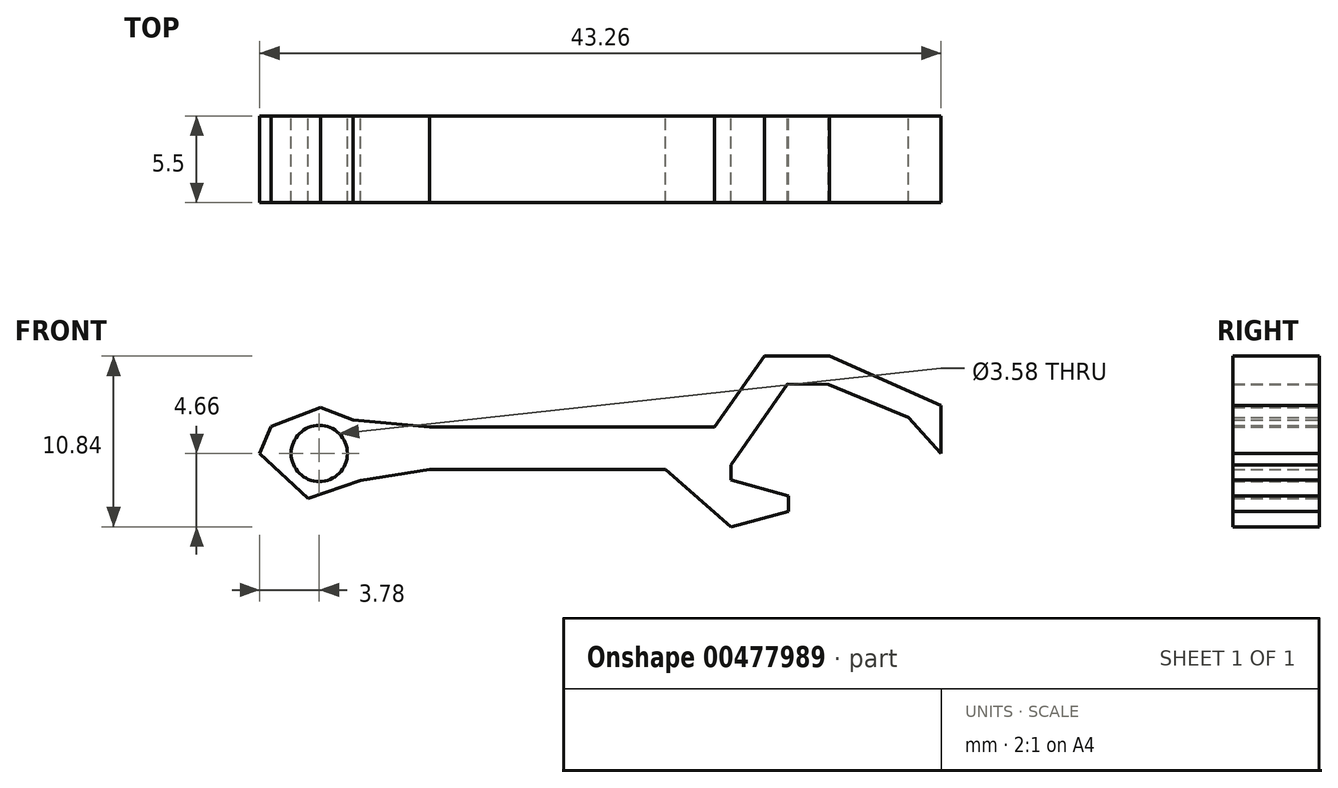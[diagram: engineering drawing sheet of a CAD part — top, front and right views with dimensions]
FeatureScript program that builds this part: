
annotation { "Feature Type Name" : "Feature", "Feature Type Description" : "" }
export const myFeature = defineFeature(function(context is Context, id is Id, definition is map)
    precondition{}
    {
        {
            var Q0;
            Q0=qCreatedBy(makeId("Front.planeOp"),FACE);
            var sketch = newSketch(context, id + "F0", { "sketchPlane" : qUnion([Q0])});
            skLineSegment(sketch, "E0", {"start": v(21.75, 0) * mm, "end": v(19.68, 2.28) * mm});
            skLineSegment(sketch, "E1", {"start": v(8.42, -0.72) * mm, "end": v(8.42, -1.68) * mm});
            skLineSegment(sketch, "E2", {"start": v(8.42, -1.68) * mm, "end": v(12.08, -2.7) * mm});
            skLineSegment(sketch, "E3", {"start": v(12.08, -2.7) * mm, "end": v(12.08, -3.68) * mm});
            skLineSegment(sketch, "E4", {"start": v(12.08, -3.68) * mm, "end": v(8.42, -4.66) * mm});
            skLineSegment(sketch, "E5", {"start": v(8.42, -4.66) * mm, "end": v(4.26, -1.03) * mm});
            skLineSegment(sketch, "E6.0", {"start": v(19.68, 2.28) * mm, "end": v(14.6, 4.38) * mm});
            skLineSegment(sketch, "E7.0", {"start": v(14.6, 4.38) * mm, "end": v(12, 4.4) * mm});
            skLineSegment(sketch, "E8", {"start": v(8.42, -0.72) * mm, "end": v(12, 4.4) * mm});
            skLineSegment(sketch, "E9", {"start": v(7.38, 1.68) * mm, "end": v(10.53, 6.18) * mm});
            skLineSegment(sketch, "E10", {"start": v(10.53, 6.18) * mm, "end": v(14.66, 6.18) * mm});
            skLineSegment(sketch, "E11", {"start": v(14.66, 6.18) * mm, "end": v(21.75, 3.05) * mm});
            skLineSegment(sketch, "E12", {"start": v(21.75, 3.05) * mm, "end": v(21.75, 0) * mm});
            skLineSegment(sketch, "E13", {"start": v(7.38, 1.68) * mm, "end": v(-10.71, 1.68) * mm});
            skLineSegment(sketch, "E14", {"start": v(4.26, -1.03) * mm, "end": v(-10.71, -1.03) * mm});
            skLineSegment(sketch, "E15", {"start": v(-17.65, 2.92) * mm, "end": v(-20.8, 1.7) * mm});
            skLineSegment(sketch, "E16", {"start": v(-20.8, 1.7) * mm, "end": v(-21.51, 0) * mm});
            skLineSegment(sketch, "E17", {"start": v(-21.51, 0) * mm, "end": v(-18.46, -2.85) * mm});
            skLineSegment(sketch, "E18", {"start": v(-18.46, -2.85) * mm, "end": v(-15.12, -1.7) * mm});
            skLineSegment(sketch, "E19", {"start": v(-15.58, 2.14) * mm, "end": v(-17.65, 2.92) * mm});
            skLineSegment(sketch, "E20", {"start": v(-15.12, -1.7) * mm, "end": v(-10.71, -1.03) * mm});
            skLineSegment(sketch, "E21", {"start": v(-15.58, 2.14) * mm, "end": v(-10.71, 1.68) * mm});
            skCircle(sketch, "E22", {"center": v(-17.73, 0) * mm, "radius": 1.79 * mm});
            skSolve(sketch);
        }
        {
            var Q0;
            Q0=makeQuery(id+"F0.imprint","IMPRINT",FACE,{"disambiguationData":[TD([[makeQuery(id+"F0.imprint","IMPRINT",EDGE,{"derivedFrom":sQuery(id+"F0.wireOp",EDGE,"E0")}),-1.0]])]});
            extrude(context, id + "F1", {"entities" : qUnion([Q0]), "depth" : 5.5 * mm});
        }
    });
